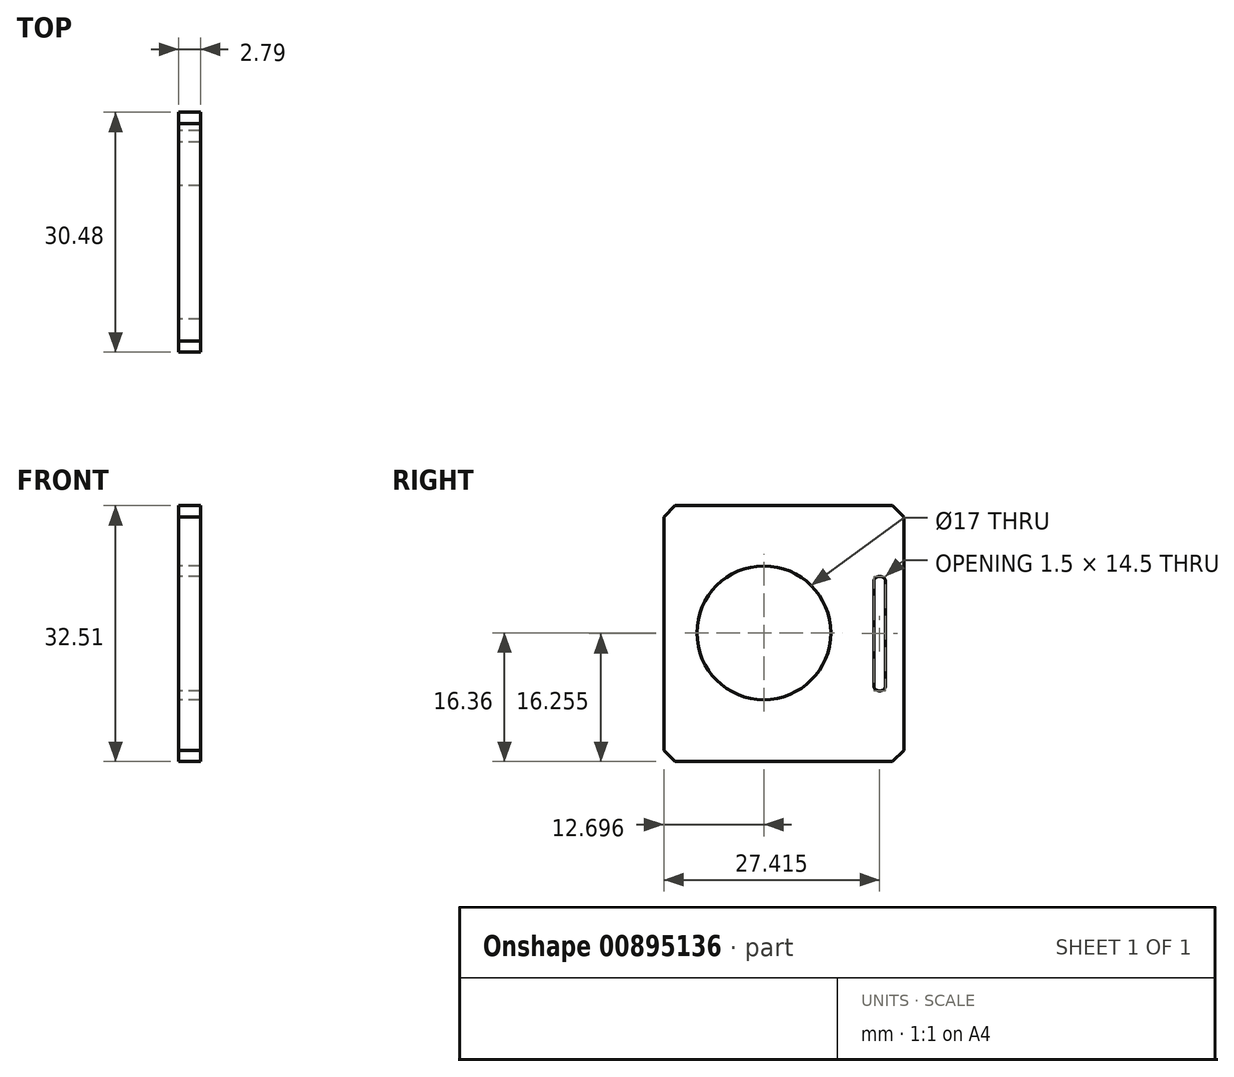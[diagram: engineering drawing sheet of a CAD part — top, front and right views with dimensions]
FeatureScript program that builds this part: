
annotation { "Feature Type Name" : "Feature", "Feature Type Description" : "" }
export const myFeature = defineFeature(function(context is Context, id is Id, definition is map)
    precondition{}
    {
        {
            var Q0;
            Q0=qCreatedBy(makeId("Right.planeOp"),FACE);
            var sketch = newSketch(context, id + "F0", { "sketchPlane" : qUnion([Q0])});
            skLineSegment(sketch, "E0.bottom", {"start": v(26.9, 27.1) * mm, "end": v(57.38, 27.1) * mm});
            skLineSegment(sketch, "E0.top", {"start": v(26.9, -5.42) * mm, "end": v(57.38, -5.42) * mm});
            skLineSegment(sketch, "E0.left", {"start": v(26.9, 27.1) * mm, "end": v(26.9, -5.42) * mm});
            skLineSegment(sketch, "E0.right", {"start": v(57.38, 27.1) * mm, "end": v(57.38, -5.42) * mm});
            skCircle(sketch, "E1", {"center": v(39.6, 10.94) * mm, "radius": 8.5 * mm});
            skPoint(sketch, "E2", {"position": v(42.14, 27.1) * mm});
            skLineSegment(sketch, "E3.bottom", {"start": v(53.57, 18.09) * mm, "end": v(55.06, 18.09) * mm});
            skLineSegment(sketch, "E3.top", {"start": v(53.57, 3.58) * mm, "end": v(55.06, 3.58) * mm});
            skLineSegment(sketch, "E3.left", {"start": v(53.57, 18.09) * mm, "end": v(53.57, 3.58) * mm});
            skLineSegment(sketch, "E3.right", {"start": v(55.06, 18.09) * mm, "end": v(55.06, 3.58) * mm});
            skPoint(sketch, "E4", {"position": v(53.57, 10.84) * mm});
            skSolve(sketch);
        }
        {
            var Q0;
            Q0 = qSketchRegion(id + "F0", true);
            extrude(context, id + "F1", {"entities" : qUnion([Q0]), "depth" : 2.8 * mm, "offsetDistance" : 25.4 * mm});
        }
        {
            var Q0;
            Q0=makeQuery(id+"F1.opExtrude","SWEPT_EDGE",EDGE,{"disambiguationData":[OSD([sQuery(id+"F0.wireOp",EDGE,"E0.bottom"),sQuery(id+"F0.wireOp",EDGE,"E0.right")])]});
            chamfer(context, id + "F2", {"entities" : qUnion([Q0]), "width" : 1.42 * mm, "tangentPropagation" : true});
        }
        {
            var Q0;
            Q0=makeQuery(id+"F1.opExtrude","SWEPT_EDGE",EDGE,{"disambiguationData":[OSD([sQuery(id+"F0.wireOp",EDGE,"E0.bottom"),sQuery(id+"F0.wireOp",EDGE,"E0.left")])]});
            chamfer(context, id + "F3", {"entities" : qUnion([Q0]), "width" : 1.42 * mm, "tangentPropagation" : true});
        }
        {
            var Q0;
            Q0=makeQuery(id+"F1.opExtrude","SWEPT_EDGE",EDGE,{"disambiguationData":[OSD([sQuery(id+"F0.wireOp",EDGE,"E0.top"),sQuery(id+"F0.wireOp",EDGE,"E0.left")])]});
            chamfer(context, id + "F4", {"entities" : qUnion([Q0]), "width" : 1.42 * mm, "tangentPropagation" : true});
        }
        {
            var Q0;
            Q0=makeQuery(id+"F1.opExtrude","SWEPT_EDGE",EDGE,{"disambiguationData":[OSD([sQuery(id+"F0.wireOp",EDGE,"E0.top"),sQuery(id+"F0.wireOp",EDGE,"E0.right")])]});
            chamfer(context, id + "F5", {"entities" : qUnion([Q0]), "width" : 1.42 * mm, "tangentPropagation" : true});
        }
        {
            var Q0;
            Q0=makeQuery(id+"F1.opExtrude","SWEPT_EDGE",EDGE,{"disambiguationData":[OSD([sQuery(id+"F0.wireOp",EDGE,"E3.top"),sQuery(id+"F0.wireOp",EDGE,"E3.left")])]});
            fillet(context, id + "F6", {"entities" : qUnion([Q0]), "radius" : 0.64 * mm, "tangentPropagation" : true, "allowEdgeOverflow" : false});
        }
        {
            var Q0;
            Q0=makeQuery(id+"F1.opExtrude","SWEPT_EDGE",EDGE,{"disambiguationData":[OSD([sQuery(id+"F0.wireOp",EDGE,"E3.top"),sQuery(id+"F0.wireOp",EDGE,"E3.right")])]});
            fillet(context, id + "F7", {"entities" : qUnion([Q0]), "radius" : 0.64 * mm, "tangentPropagation" : true, "allowEdgeOverflow" : false});
        }
        {
            var Q0;
            Q0=makeQuery(id+"F1.opExtrude","SWEPT_EDGE",EDGE,{"disambiguationData":[OSD([sQuery(id+"F0.wireOp",EDGE,"E3.bottom"),sQuery(id+"F0.wireOp",EDGE,"E3.left")])]});
            fillet(context, id + "F8", {"entities" : qUnion([Q0]), "radius" : 0.64 * mm, "tangentPropagation" : true, "allowEdgeOverflow" : false});
        }
        {
            var Q0;
            Q0=makeQuery(id+"F1.opExtrude","SWEPT_EDGE",EDGE,{"disambiguationData":[OSD([sQuery(id+"F0.wireOp",EDGE,"E3.bottom"),sQuery(id+"F0.wireOp",EDGE,"E3.right")])]});
            fillet(context, id + "F9", {"entities" : qUnion([Q0]), "radius" : 0.64 * mm, "tangentPropagation" : true, "allowEdgeOverflow" : false});
        }
    });
